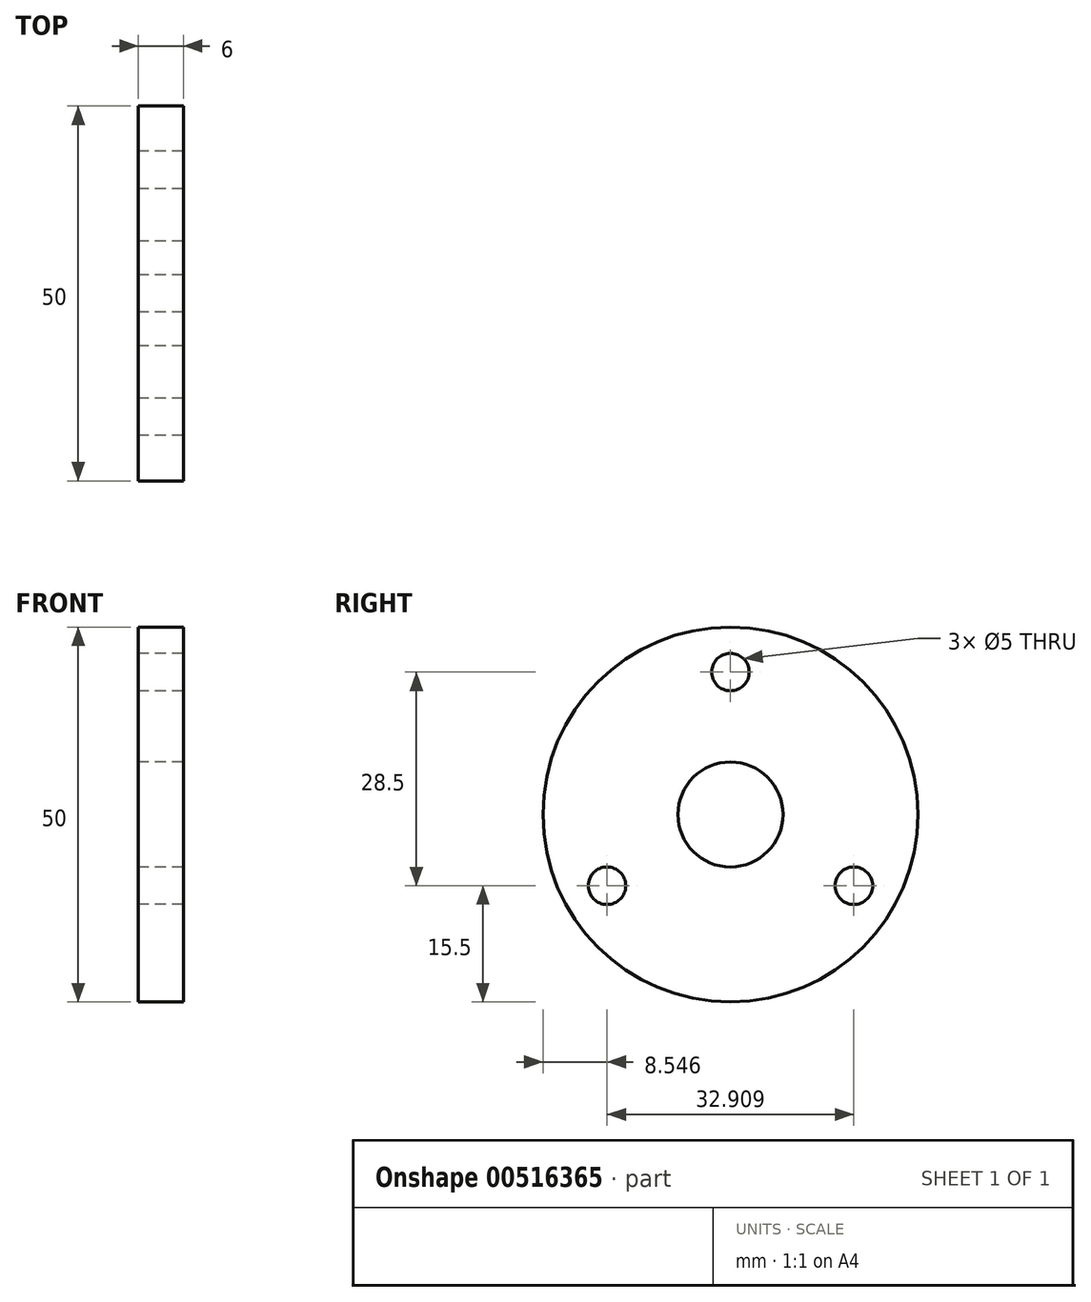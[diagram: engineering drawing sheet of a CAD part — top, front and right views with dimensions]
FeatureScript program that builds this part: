
annotation { "Feature Type Name" : "Feature", "Feature Type Description" : "" }
export const myFeature = defineFeature(function(context is Context, id is Id, definition is map)
    precondition{}
    {
        {
            var Q0;
            Q0=qCreatedBy(makeId("Right.planeOp"),FACE);
            var sketch = newSketch(context, id + "F0", { "sketchPlane" : qUnion([Q0])});
            skCircle(sketch, "E0", {"center": v(0, 0) * mm, "radius": 25 * mm});
            skCircle(sketch, "E1", {"center": v(0, 0) * mm, "radius": 7 * mm});
            skPoint(sketch, "E2", {"position": v(0, 19) * mm});
            skCircle(sketch, "E3", {"center": v(0, 19) * mm, "radius": 2.5 * mm});
            skCircle(sketch, "E4", {"center": v(-16.45, -9.5) * mm, "radius": 2.5 * mm});
            skCircle(sketch, "E5", {"center": v(16.45, -9.5) * mm, "radius": 2.5 * mm});
            skSolve(sketch);
        }
        {
            var Q0;
            Q0 = qSketchRegion(id + "F0", true);
            extrude(context, id + "F1", {"entities" : qUnion([Q0]), "depth" : 6 * mm, "offsetDistance" : 25 * mm});
        }
    });
